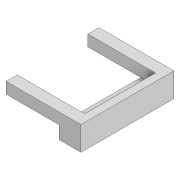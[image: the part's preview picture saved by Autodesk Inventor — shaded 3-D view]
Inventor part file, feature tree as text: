
AUTODESK INVENTOR PART (.ipt)
format: ipt  version: 2021 (Build 250183000, 183)  size: 139,776 bytes
history: native  units: mm
features: extrude x5, sketch x5, projected_geometry x3
ambient origin geometry x8: Origin, YZ Plane, XZ Plane, XY Plane, X Axis, Y Axis, Z Axis, Center Point
bodies: Volumenkörper1 (feature_tree)
feature tree (13):
  extrude  "Extrusion1"  Depth=18.21mm
  extrude  "Extrusion2"  Depth=3.91mm
  extrude  "Extrusion3"  Depth=19.1mm
  extrude  "Extrusion4"  Depth=3.0mm
  extrude  "Extrusion5"  Depth=3.0mm
  sketch  "Skizze1"  dims[d0=18.21mm d1=24.0mm]
  sketch  "Skizze2"  dims[d2=3.5mm d3=0.0mm d4=3.91mm]
  projected_geometry  "Projizierte Kontur1"
  sketch  "Skizze3"  dims[d5=0.0mm d6=0.0mm d7=19.1mm]
  sketch  "Skizze4"  dims[d8=18.21mm d9=3.0mm]
  projected_geometry  "Projizierte Kontur2"
  projected_geometry  "Projizierte Kontur3"
  sketch  "Skizze5"  dims[d10=18.21mm d11=3.0mm d12=3.0mm d13=0.0mm d14=3.0mm d15=0.0mm d16=2.0mm d17=0.0mm]
